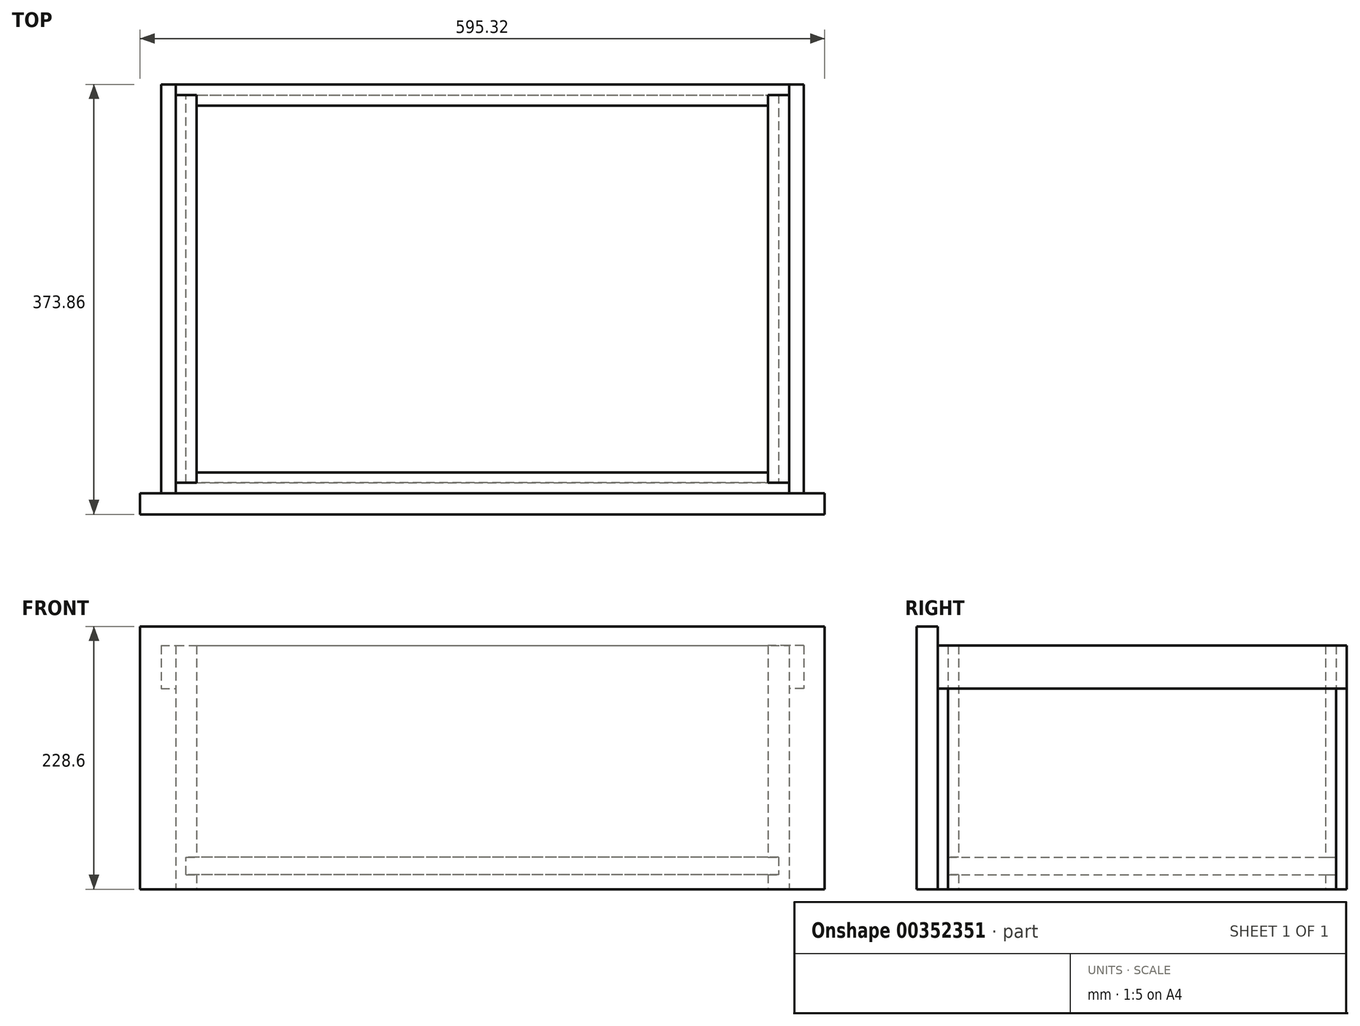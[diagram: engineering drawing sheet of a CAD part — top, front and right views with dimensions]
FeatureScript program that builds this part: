
annotation { "Feature Type Name" : "Feature", "Feature Type Description" : "" }
export const myFeature = defineFeature(function(context is Context, id is Id, definition is map)
    precondition{}
    {
        {
            var Q0;
            Q0=qCreatedBy(makeId("Top.planeOp"),FACE);
            var sketch = newSketch(context, id + "F0", { "sketchPlane" : qUnion([Q0])});
            skLineSegment(sketch, "E0.top", {"start": v(-266.7, -177.8) * mm, "end": v(266.7, -177.8) * mm, "construction": true});
            skLineSegment(sketch, "E0.left", {"start": v(-266.7, -177.8) * mm, "end": v(-266.7, 177.8) * mm, "construction": true});
            skLineSegment(sketch, "E0.right", {"start": v(266.7, -177.8) * mm, "end": v(266.7, 177.8) * mm, "construction": true});
            skLineSegment(sketch, "E1", {"start": v(-266.7, 177.8) * mm, "end": v(266.7, 177.8) * mm, "construction": true});
            skLineSegment(sketch, "E2", {"start": v(-266.7, 177.8) * mm, "end": v(-266.7, 168.67) * mm});
            skLineSegment(sketch, "E3", {"start": v(-266.7, 168.67) * mm, "end": v(-248.44, 168.67) * mm});
            skLineSegment(sketch, "E4", {"start": v(-248.44, 168.67) * mm, "end": v(-248.44, 159.54) * mm});
            skLineSegment(sketch, "E5.MirrorCS", {"start": v(266.7, 177.8) * mm, "end": v(266.7, 168.67) * mm});
            skLineSegment(sketch, "E6.MirrorCS", {"start": v(248.44, 168.67) * mm, "end": v(248.44, 159.54) * mm});
            skLineSegment(sketch, "E7.MirrorCS", {"start": v(266.7, 168.67) * mm, "end": v(248.44, 168.67) * mm});
            skLineSegment(sketch, "E8", {"start": v(-266.7, 177.8) * mm, "end": v(266.7, 177.8) * mm});
            skLineSegment(sketch, "E9", {"start": v(-248.44, 159.54) * mm, "end": v(248.44, 159.54) * mm});
            skLineSegment(sketch, "E10.MirrorCS", {"start": v(266.7, -177.8) * mm, "end": v(266.7, -168.67) * mm});
            skLineSegment(sketch, "E11.MirrorCS", {"start": v(-266.7, -177.8) * mm, "end": v(-266.7, -168.67) * mm});
            skLineSegment(sketch, "E12.MirrorCS", {"start": v(248.44, -168.67) * mm, "end": v(248.44, -159.54) * mm});
            skLineSegment(sketch, "E13.MirrorCS", {"start": v(266.7, -168.67) * mm, "end": v(248.44, -168.67) * mm});
            skLineSegment(sketch, "E14.MirrorCS", {"start": v(-248.44, -168.67) * mm, "end": v(-248.44, -159.54) * mm});
            skLineSegment(sketch, "E15.MirrorCS", {"start": v(-266.7, -168.67) * mm, "end": v(-248.44, -168.67) * mm});
            skLineSegment(sketch, "E16.MirrorCS", {"start": v(-266.7, -177.8) * mm, "end": v(266.7, -177.8) * mm});
            skLineSegment(sketch, "E17.MirrorCS", {"start": v(-248.44, -159.54) * mm, "end": v(248.44, -159.54) * mm});
            skLineSegment(sketch, "E18", {"start": v(-297.66, 177.8) * mm, "end": v(-297.66, -177.8) * mm, "construction": true});
            skLineSegment(sketch, "E19.MirrorCS", {"start": v(297.66, 177.8) * mm, "end": v(297.66, -177.8) * mm, "construction": true});
            skSolve(sketch);
        }
        {
            var Q0;
            Q0=qCreatedBy(makeId("Top.planeOp"),FACE);
            var sketch = newSketch(context, id + "F1", { "sketchPlane" : qUnion([Q0])});
            skLineSegment(sketch, "E20.bottom", {"start": v(-266.7, 168.67) * mm, "end": v(-248.44, 168.67) * mm});
            skLineSegment(sketch, "E20.top", {"start": v(-266.7, -168.67) * mm, "end": v(-248.44, -168.67) * mm});
            skLineSegment(sketch, "E20.left", {"start": v(-266.7, 168.67) * mm, "end": v(-266.7, -168.67) * mm});
            skLineSegment(sketch, "E20.right", {"start": v(-248.44, 168.67) * mm, "end": v(-248.44, -168.67) * mm});
            skLineSegment(sketch, "E21.MirrorCS", {"start": v(248.44, 168.67) * mm, "end": v(248.44, -168.67) * mm});
            skLineSegment(sketch, "E22.MirrorCS", {"start": v(266.7, 168.67) * mm, "end": v(266.7, -168.67) * mm});
            skLineSegment(sketch, "E23.MirrorCS", {"start": v(266.7, 168.67) * mm, "end": v(248.44, 168.67) * mm});
            skLineSegment(sketch, "E24.MirrorCS", {"start": v(266.7, -168.67) * mm, "end": v(248.44, -168.67) * mm});
            skSolve(sketch);
        }
        {
            var Q0;
            Q0=qCreatedBy(makeId("Top.planeOp"),FACE);
            var sketch = newSketch(context, id + "F2", { "sketchPlane" : qUnion([Q0])});
            skLineSegment(sketch, "E25.bottom", {"start": v(-297.66, -196.06) * mm, "end": v(297.66, -196.06) * mm});
            skLineSegment(sketch, "E25.top", {"start": v(-297.66, -177.8) * mm, "end": v(297.66, -177.8) * mm});
            skLineSegment(sketch, "E25.left", {"start": v(-297.66, -196.06) * mm, "end": v(-297.66, -177.8) * mm});
            skLineSegment(sketch, "E25.right", {"start": v(297.66, -196.06) * mm, "end": v(297.66, -177.8) * mm});
            skSolve(sketch);
        }
        {
            var Q0;
            Q0=qCreatedBy(makeId("Front.planeOp"),FACE);
            var sketch = newSketch(context, id + "F3", { "sketchPlane" : qUnion([Q0])});
            skLineSegment(sketch, "E26.bottom", {"start": v(-257.57, 27.78) * mm, "end": v(257.57, 27.78) * mm});
            skLineSegment(sketch, "E26.top", {"start": v(-257.57, 12.7) * mm, "end": v(257.57, 12.7) * mm});
            skLineSegment(sketch, "E26.left", {"start": v(-257.57, 27.78) * mm, "end": v(-257.57, 12.7) * mm});
            skLineSegment(sketch, "E26.right", {"start": v(257.57, 27.78) * mm, "end": v(257.57, 12.7) * mm});
            skSolve(sketch);
        }
        {
            var Q0;
            Q0=qCreatedBy(makeId("Front.planeOp"),FACE);
            var sketch = newSketch(context, id + "F4", { "sketchPlane" : qUnion([Q0])});
            skLineSegment(sketch, "E27.bottom", {"start": v(-279.4, 211.93) * mm, "end": v(-266.7, 211.93) * mm});
            skLineSegment(sketch, "E27.top", {"start": v(-279.4, 174.62) * mm, "end": v(-266.7, 174.62) * mm});
            skLineSegment(sketch, "E27.left", {"start": v(-279.4, 211.93) * mm, "end": v(-279.4, 174.62) * mm});
            skLineSegment(sketch, "E27.right", {"start": v(-266.7, 211.93) * mm, "end": v(-266.7, 174.62) * mm});
            skLineSegment(sketch, "E28.MirrorCS", {"start": v(279.4, 174.62) * mm, "end": v(266.7, 174.62) * mm});
            skLineSegment(sketch, "E29.MirrorCS", {"start": v(279.4, 211.93) * mm, "end": v(266.7, 211.93) * mm});
            skLineSegment(sketch, "E30.MirrorCS", {"start": v(279.4, 211.93) * mm, "end": v(279.4, 174.62) * mm});
            skLineSegment(sketch, "E31.MirrorCS", {"start": v(266.7, 211.93) * mm, "end": v(266.7, 174.62) * mm});
            skSolve(sketch);
        }
        {
            var Q0;
            Q0=makeQuery(id+"F0.imprint","IMPRINT",FACE,{"disambiguationData":[TD([[makeQuery(id+"F0.imprint","IMPRINT",EDGE,{"derivedFrom":sQuery(id+"F0.wireOp",EDGE,"E2")}),1.0]])]});
            var Q1;
            Q1=makeQuery(id+"F0.imprint","IMPRINT",FACE,{"disambiguationData":[TD([[makeQuery(id+"F0.imprint","IMPRINT",EDGE,{"derivedFrom":sQuery(id+"F0.wireOp",EDGE,"E10.MirrorCS")}),1.0]])]});
            extrude(context, id + "F5", {"entities" : qUnion([Q0, Q1]), "depth" : 211.93 * mm});
        }
        {
            var Q0;
            Q0=makeQuery(id+"F1.imprint","IMPRINT",FACE,{"disambiguationData":[TD([[makeQuery(id+"F1.imprint","IMPRINT",EDGE,{"derivedFrom":sQuery(id+"F1.wireOp",EDGE,"E20.bottom")}),-1.0]])]});
            var Q1;
            Q1=makeQuery(id+"F1.imprint","IMPRINT",FACE,{"disambiguationData":[TD([[makeQuery(id+"F1.imprint","IMPRINT",EDGE,{"derivedFrom":sQuery(id+"F1.wireOp",EDGE,"E21.MirrorCS")}),1.0]])]});
            var Q2;
            Q2=makeQuery(id+"F5.opExtrude","CAP_FACE",FACE,{"disambiguationData":[OSD([sQuery(id+"F0.wireOp",EDGE,"E2"),sQuery(id+"F0.wireOp",EDGE,"E3"),sQuery(id+"F0.wireOp",EDGE,"E4"),sQuery(id+"F0.wireOp",EDGE,"E5.MirrorCS"),sQuery(id+"F0.wireOp",EDGE,"E6.MirrorCS"),sQuery(id+"F0.wireOp",EDGE,"E7.MirrorCS"),sQuery(id+"F0.wireOp",EDGE,"E8"),sQuery(id+"F0.wireOp",EDGE,"E9")])],"isStart":false});
            extrude(context, id + "F6", {"entities" : qUnion([Q0, Q1]), "endBound" : BoundingType.UP_TO_SURFACE, "endBoundEntityFace" : qUnion([Q2]), "depth" : 228.6 * mm});
        }
        {
            var Q0;
            Q0=makeQuery(id+"F2.imprint","IMPRINT",FACE,{"disambiguationData":[TD([[makeQuery(id+"F2.imprint","IMPRINT",EDGE,{"derivedFrom":sQuery(id+"F2.wireOp",EDGE,"E25.bottom")}),1.0]])]});
            extrude(context, id + "F7", {"entities" : qUnion([Q0]), "depth" : 228.6 * mm});
        }
        {
            var Q0;
            Q0=qSketchRegion(id+"F3",true);
            var Q1;
            Q1=makeQuery(id+"F5.opExtrude","SWEPT_FACE",FACE,{"disambiguationData":[OSD([sQuery(id+"F0.wireOp",EDGE,"E13.MirrorCS")])]});
            var Q2;
            Q2=makeQuery(id+"F5.opExtrude","SWEPT_FACE",FACE,{"disambiguationData":[OSD([sQuery(id+"F0.wireOp",EDGE,"E7.MirrorCS")])]});
            extrude(context, id + "F8", {"entities" : qUnion([Q0]), "operationType" : NewBodyOperationType.REMOVE, "oppositeDirection" : true, "endBoundEntityFace" : qUnion([Q1]), "depth" : 168.67 * mm, "hasSecondDirection" : true, "secondDirectionOppositeDirection" : false, "secondDirectionBoundEntityFace" : qUnion([Q2]), "secondDirectionDepth" : 168.67 * mm});
        }
        {
            var Q0;
            Q0=qSketchRegion(id+"F3",true);
            var Q1;
            Q1=makeQuery(id+"F8.boolean.opBoolean","MERGE",FACE,{"derivedFrom":[makeQuery(id+"F5.opExtrude","SWEPT_FACE",FACE,{"disambiguationData":[OSD([sQuery(id+"F0.wireOp",EDGE,"E13.MirrorCS")])]}),makeQuery(id+"F5.opExtrude","SWEPT_FACE",FACE,{"disambiguationData":[OSD([sQuery(id+"F0.wireOp",EDGE,"E15.MirrorCS")])]}),makeQuery(id+"F8.opExtrude","CAP_FACE",FACE,{"disambiguationData":[OSD([sQuery(id+"F3.wireOp",EDGE,"E26.bottom"),sQuery(id+"F3.wireOp",EDGE,"E26.top"),sQuery(id+"F3.wireOp",EDGE,"E26.left"),sQuery(id+"F3.wireOp",EDGE,"E26.right")])],"isStart":true})]});
            var Q2;
            Q2=makeQuery(id+"F8.boolean.opBoolean","MERGE",FACE,{"derivedFrom":[makeQuery(id+"F5.opExtrude","SWEPT_FACE",FACE,{"disambiguationData":[OSD([sQuery(id+"F0.wireOp",EDGE,"E3")])]}),makeQuery(id+"F5.opExtrude","SWEPT_FACE",FACE,{"disambiguationData":[OSD([sQuery(id+"F0.wireOp",EDGE,"E7.MirrorCS")])]}),makeQuery(id+"F8.opExtrude","CAP_FACE",FACE,{"disambiguationData":[OSD([sQuery(id+"F3.wireOp",EDGE,"E26.bottom"),sQuery(id+"F3.wireOp",EDGE,"E26.top"),sQuery(id+"F3.wireOp",EDGE,"E26.left"),sQuery(id+"F3.wireOp",EDGE,"E26.right")])],"isStart":false})]});
            extrude(context, id + "F9", {"entities" : qUnion([Q0]), "endBound" : BoundingType.UP_TO_SURFACE, "endBoundEntityFace" : qUnion([Q1]), "depth" : 25.4 * mm, "hasSecondDirection" : true, "secondDirectionBound" : SecondDirectionBoundingType.UP_TO_SURFACE, "secondDirectionOppositeDirection" : true, "secondDirectionBoundEntityFace" : qUnion([Q2]), "secondDirectionDepth" : 25.4 * mm});
        }
        {
            var Q0;
            Q0=qSketchRegion(id+"F4",true);
            extrude(context, id + "F10", {"entities" : qUnion([Q0]), "depth" : 177.8 * mm, "hasSecondDirection" : true, "secondDirectionOppositeDirection" : true, "secondDirectionDepth" : 177.8 * mm});
        }
    });
